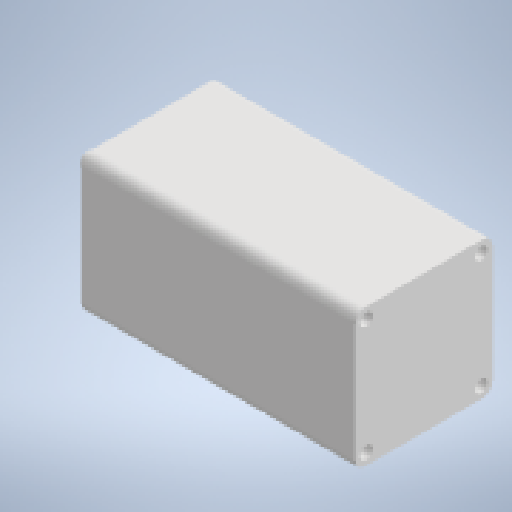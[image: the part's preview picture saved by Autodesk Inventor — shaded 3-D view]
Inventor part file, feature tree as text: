
AUTODESK INVENTOR PART (.ipt)
format: ipt  version: 2023 (Build 270158000, 158)  size: 152,576 bytes
history: native  units: mm
features: extrude x3, sketch x3
ambient origin geometry x8: Origin, YZ Plane, XZ Plane, XY Plane, X Axis, Y Axis, Z Axis, Center Point
bodies: Solid1 (feature_tree)
feature tree (6):
  extrude  "Extrusion1"  Depth=56.4mm
  extrude  "Extrusion2"  Depth=4.0mm
  extrude  "Extrusion3"  Depth=4.0mm
  sketch  "Sketch1"  dims[d0=56.4mm d1=47.14mm]
  sketch  "Sketch2"  dims[d2=5.0mm d3=4.0mm]
  sketch  "Sketch3"  dims[d4=4.0mm d5=4.0mm d6=4.0mm d7=112.0mm d8=0.0mm d9=38.1mm d10=1.6mm d11=0.0mm d12=10.0mm d13=24.0mm d14=0.0mm]
